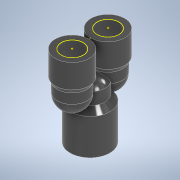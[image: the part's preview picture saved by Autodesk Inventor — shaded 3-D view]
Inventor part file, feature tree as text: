
AUTODESK INVENTOR PART (.ipt)
format: ipt  version: 2022 (Build 260153000, 153)  size: 237,568 bytes
history: native  units: mm
features: sketch x15, extrude x6, projected_geometry x6, plane x3, loft x3, revolve x3, other x3
ambient origin geometry x8: Origin, YZ Plane, XZ Plane, XY Plane, X Axis, Y Axis, Z Axis, Center Point
bodies: Solid1 (feature_tree)
feature tree (39):
  extrude  "Extrusion1"  Depth=18.0mm TaperAngle=0.0deg
  plane  "Work Plane1"
  extrude  "Extrusion2"  Depth=9.0mm
  plane  "Work Plane2"
  loft  "Loft1"
  loft  "Loft2"
  plane  "Work Plane3"
  loft  "Loft3"
  extrude  "Extrusion3"  TaperAngle=0.0deg  [1 undecoded]
  extrude  "Extrusion4"  TaperAngle=0.0deg  [1 undecoded]
  revolve  "Revolution1"  [1 undecoded]
  revolve  "Revolution2"  Angle=90.0deg
  revolve  "Revolution3"  [1 undecoded]
  extrude  "Extrusion5"  Depth=4.0mm
  extrude  "Extrusion6"  TaperAngle=90.0deg  [1 undecoded]
  sketch  "Sketch14"  dims[d35=7.5mm]
  sketch  "Sketch15"  dims[d36=7.5mm]
  sketch  "Sketch16"  dims[d37=7.5mm d38=90.0deg d39=7.5mm d40=7.5mm d41=7.5mm d42=90.0deg d43=11.0mm d44=11.0mm d45=14.0mm d46=0.0mm d47=13.0mm d48=18.0mm d49=0.0mm]
  sketch  "Sketch1"  dims[d0=20.0mm d1=18.0mm d2=0.0mm]
  sketch  "Sketch2"  dims[d3=-45.0mm d4=9.0mm]
  sketch  "Sketch3"  dims[d5=18.0mm d6=17.0mm]
  other  "Edges1"
  sketch  "Sketch4"  dims[d7=17.0mm d8=12.0mm d9=0.0mm]
  projected_geometry  "Projected Loop1"
  other  "Edges2"
  sketch  "Sketch5"  dims[d10=2.0mm d11=15.0mm]
  other  "Edges3"
  sketch  "Sketch6"  dims[d13=0.0mm d14=90.0deg d15=0.0mm d16=90.0deg]
  projected_geometry  "Projected Loop2"
  sketch  "Sketch7"  dims[d17=15.0mm d18=0.0mm d19=90.0deg]
  projected_geometry  "Projected Loop3"
  projected_geometry  "Projected Loop4"
  sketch  "Sketch8"  dims[d20=0.0mm d21=90.0deg d22=3.0mm]
  sketch  "Sketch10"  dims[d23=15.0mm d24=0.0mm d25=90.0deg]
  projected_geometry  "Projected Loop5"
  sketch  "Sketch11"  dims[d26=0.0mm d27=90.0deg d28=6.0mm d29=0.0mm]
  sketch  "Sketch12"  dims[d30=5.0mm d31=0.0mm d32=4.0mm]
  projected_geometry  "Projected Loop6"
  sketch  "Sketch13"  dims[d33=8.5mm d34=90.0deg]
note: 5 required parameter values undecoded (feature->parameter linkage not recoverable at this tier; creation-order binding heuristic only, values carry confidence <= 0.55)